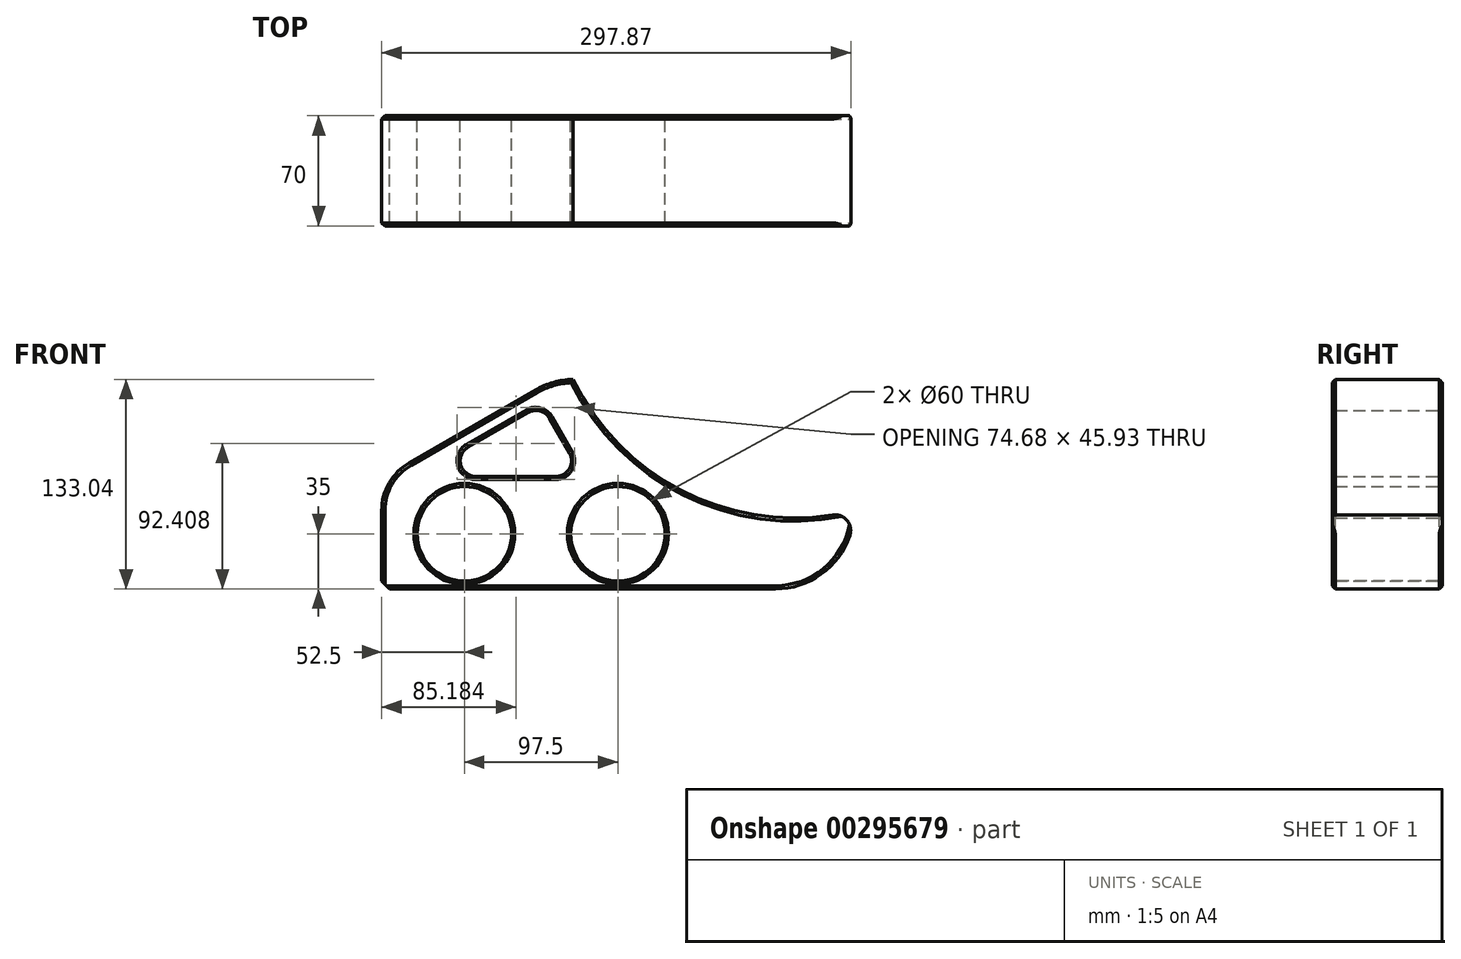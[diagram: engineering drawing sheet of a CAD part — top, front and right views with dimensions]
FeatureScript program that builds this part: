
annotation { "Feature Type Name" : "Feature", "Feature Type Description" : "" }
export const myFeature = defineFeature(function(context is Context, id is Id, definition is map)
    precondition{}
    {
        {
            var Q0;
            Q0=qCreatedBy(makeId("Front.planeOp"),FACE);
            var sketch = newSketch(context, id + "F0", { "sketchPlane" : qUnion([Q0])});
            skLineSegment(sketch, "E0", {"start": v(-157.76, 0) * mm, "end": v(158.79, 0) * mm, "construction": true});
            skLineSegment(sketch, "E1.bottom", {"start": v(150, -35) * mm, "end": v(-150, -35) * mm});
            skLineSegment(sketch, "E1.left", {"start": v(150, -35) * mm, "end": v(150, 14.8) * mm});
            skLineSegment(sketch, "E1.right", {"start": v(-150, -35) * mm, "end": v(-150, 14.8) * mm});
            skPoint(sketch, "E1.middle", {"position": v(0, 0) * mm});
            skCircle(sketch, "E2", {"center": v(0, 0) * mm, "radius": 30 * mm});
            skLineSegment(sketch, "E3", {"start": v(-132.5, 45.1) * mm, "end": v(-52.4, 91.35) * mm});
            skArc(sketch, "E4.filletArc", {"start": v(-132.5, 45.1) * mm, "mid": v(-145.31, 32.3) * mm, "end": v(-150, 14.8) * mm});
            skPoint(sketch, "E5.visualSharp", {"position": v(-41.9, 97.42) * mm});
            skArc(sketch, "E5.filletArc", {"start": v(-28.5, 98.04) * mm, "mid": v(-40.87, 96.2) * mm, "end": v(-52.4, 91.35) * mm});
            skLineSegment(sketch, "E6", {"start": v(0, 102.38) * mm, "end": v(0, -61.25) * mm, "construction": true});
            skLineSegment(sketch, "E7", {"start": v(0, 0) * mm, "end": v(-97.5, 0) * mm, "construction": true});
            skPoint(sketch, "E8", {"position": v(-97.5, 0) * mm});
            skCircle(sketch, "E9", {"center": v(-97.5, 0) * mm, "radius": 30 * mm});
            skLineSegment(sketch, "E10.0", {"start": v(-95.18, 55.1) * mm, "end": v(-57.15, 77.06) * mm});
            skLineSegment(sketch, "E11", {"start": v(-43.5, 73.4) * mm, "end": v(-30.82, 51.44) * mm});
            skLineSegment(sketch, "E12", {"start": v(-90.18, 36.44) * mm, "end": v(-39.48, 36.44) * mm});
            skPoint(sketch, "E13.visualSharp", {"position": v(-48.5, 82.06) * mm});
            skArc(sketch, "E13.filletArc", {"start": v(-43.5, 73.4) * mm, "mid": v(-49.57, 78.06) * mm, "end": v(-57.15, 77.06) * mm});
            skArc(sketch, "E14.filletArc", {"start": v(-39.48, 36.44) * mm, "mid": v(-30.82, 41.44) * mm, "end": v(-30.82, 51.44) * mm});
            skPoint(sketch, "E15.visualSharp", {"position": v(0, 38.68) * mm});
            skPoint(sketch, "E16.newPointA", {"position": v(48.5, 82.06) * mm});
            skPoint(sketch, "E17.visualSharp", {"position": v(-127.5, 36.44) * mm});
            skArc(sketch, "E17.filletArc", {"start": v(-95.18, 55.1) * mm, "mid": v(-99.84, 43.86) * mm, "end": v(-90.18, 36.44) * mm});
            skPoint(sketch, "E18.visualSharp", {"position": v(127.5, 36.44) * mm});
            skArc(sketch, "E19", {"start": v(-28.5, 98.04) * mm, "mid": v(45.97, 24.73) * mm, "end": v(150, 14.8) * mm});
            skSolve(sketch);
        }
        {
            var Q0;
            Q0 = qSketchRegion(id + "F0", true);
            extrude(context, id + "F1", {"entities" : qUnion([Q0]), "depth" : 70 * mm, "symmetric" : true});
        }
        {
            var Q0;
            Q0=makeQuery(id+"F1.opExtrude","SWEPT_EDGE",EDGE,{"disambiguationData":[OSD([sQuery(id+"F0.wireOp",EDGE,"E1.bottom"),sQuery(id+"F0.wireOp",EDGE,"E1.left")])]});
            fillet(context, id + "F2", {"entities" : qUnion([Q0]), "radius" : 50 * mm, "tangentPropagation" : true, "allowEdgeOverflow" : false});
        }
        {
            var Q0;
            Q0=makeQuery(id+"F1.opExtrude","CAP_FACE",FACE,{"disambiguationData":[OSD([sQuery(id+"F0.wireOp",EDGE,"E1.bottom"),sQuery(id+"F0.wireOp",EDGE,"E1.left"),sQuery(id+"F0.wireOp",EDGE,"E1.right"),sQuery(id+"F0.wireOp",EDGE,"E2"),sQuery(id+"F0.wireOp",EDGE,"E3"),sQuery(id+"F0.wireOp",EDGE,"E4.filletArc"),sQuery(id+"F0.wireOp",EDGE,"E5.filletArc"),sQuery(id+"F0.wireOp",EDGE,"2128d712-c22e-43d0-b137-ae846bd3470c0.MirrorCS"),sQuery(id+"F0.wireOp",EDGE,"ead384d1-ae69-4692-b830-1a13f9f5a69b0.MirrorCS"),sQuery(id+"F0.wireOp",EDGE,"37f9a7ff-8684-4468-8a72-e05079eaa0670.MirrorCS"),sQuery(id+"F0.wireOp",EDGE,"Lrirhn2S-7brx-2jdC-clf1-sQWSoA0U2pV4"),sQuery(id+"F0.wireOp",EDGE,"E9"),sQuery(id+"F0.wireOp",EDGE,"E10.0"),sQuery(id+"F0.wireOp",EDGE,"fc2dcb0f-4b4e-4361-bf83-8e2945b27883.0"),sQuery(id+"F0.wireOp",EDGE,"da70da69-e66b-4109-82d2-453cd6daba01.0"),sQuery(id+"F0.wireOp",EDGE,"AouGleSv-KkGm-sB8C-ZEsv-O4xofjI2ggc6"),sQuery(id+"F0.wireOp",EDGE,"E11"),sQuery(id+"F0.wireOp",EDGE,"E12"),sQuery(id+"F0.wireOp",EDGE,"ibZBRqrK-dixR-fJSc-eGvf-ZQZpcMRPZl58"),sQuery(id+"F0.wireOp",EDGE,"4ea5772b-329a-4e50-88f7-68c20ca4a20b0.MirrorCS"),sQuery(id+"F0.wireOp",EDGE,"01e6399d-9f67-49b3-929a-f7497086e1730.MirrorCS"),sQuery(id+"F0.wireOp",EDGE,"E13.filletArc"),sQuery(id+"F0.wireOp",EDGE,"E14.filletArc"),sQuery(id+"F0.wireOp",EDGE,"E15.filletArc"),sQuery(id+"F0.wireOp",EDGE,"7a9b99ec-dd7e-44b2-9577-c392ffdbf900.filletArc"),sQuery(id+"F0.wireOp",EDGE,"3fdbf697-db4c-413a-9f31-464b24b49e91.filletArc"),sQuery(id+"F0.wireOp",EDGE,"E16.filletArc"),sQuery(id+"F0.wireOp",EDGE,"00bd977d-d024-4b05-abdb-e15cf0350885.filletArc"),sQuery(id+"F0.wireOp",EDGE,"E17.filletArc"),sQuery(id+"F0.wireOp",EDGE,"E18.filletArc")])],"isStart":false});
            var Q1;
            Q1=makeQuery(id+"F1.opExtrude","CAP_FACE",FACE,{"disambiguationData":[OSD([sQuery(id+"F0.wireOp",EDGE,"E1.bottom"),sQuery(id+"F0.wireOp",EDGE,"E1.left"),sQuery(id+"F0.wireOp",EDGE,"E1.right"),sQuery(id+"F0.wireOp",EDGE,"E2"),sQuery(id+"F0.wireOp",EDGE,"E3"),sQuery(id+"F0.wireOp",EDGE,"E4.filletArc"),sQuery(id+"F0.wireOp",EDGE,"E5.filletArc"),sQuery(id+"F0.wireOp",EDGE,"2128d712-c22e-43d0-b137-ae846bd3470c0.MirrorCS"),sQuery(id+"F0.wireOp",EDGE,"ead384d1-ae69-4692-b830-1a13f9f5a69b0.MirrorCS"),sQuery(id+"F0.wireOp",EDGE,"37f9a7ff-8684-4468-8a72-e05079eaa0670.MirrorCS"),sQuery(id+"F0.wireOp",EDGE,"Lrirhn2S-7brx-2jdC-clf1-sQWSoA0U2pV4"),sQuery(id+"F0.wireOp",EDGE,"E9"),sQuery(id+"F0.wireOp",EDGE,"E10.0"),sQuery(id+"F0.wireOp",EDGE,"fc2dcb0f-4b4e-4361-bf83-8e2945b27883.0"),sQuery(id+"F0.wireOp",EDGE,"da70da69-e66b-4109-82d2-453cd6daba01.0"),sQuery(id+"F0.wireOp",EDGE,"AouGleSv-KkGm-sB8C-ZEsv-O4xofjI2ggc6"),sQuery(id+"F0.wireOp",EDGE,"E11"),sQuery(id+"F0.wireOp",EDGE,"E12"),sQuery(id+"F0.wireOp",EDGE,"ibZBRqrK-dixR-fJSc-eGvf-ZQZpcMRPZl58"),sQuery(id+"F0.wireOp",EDGE,"4ea5772b-329a-4e50-88f7-68c20ca4a20b0.MirrorCS"),sQuery(id+"F0.wireOp",EDGE,"01e6399d-9f67-49b3-929a-f7497086e1730.MirrorCS"),sQuery(id+"F0.wireOp",EDGE,"E13.filletArc"),sQuery(id+"F0.wireOp",EDGE,"E14.filletArc"),sQuery(id+"F0.wireOp",EDGE,"E15.filletArc"),sQuery(id+"F0.wireOp",EDGE,"7a9b99ec-dd7e-44b2-9577-c392ffdbf900.filletArc"),sQuery(id+"F0.wireOp",EDGE,"3fdbf697-db4c-413a-9f31-464b24b49e91.filletArc"),sQuery(id+"F0.wireOp",EDGE,"E16.filletArc"),sQuery(id+"F0.wireOp",EDGE,"00bd977d-d024-4b05-abdb-e15cf0350885.filletArc"),sQuery(id+"F0.wireOp",EDGE,"E17.filletArc"),sQuery(id+"F0.wireOp",EDGE,"E18.filletArc")])],"isStart":true});
            chamfer(context, id + "F3", {"entities" : qUnion([Q0, Q1]), "width" : 2 * mm, "tangentPropagation" : true});
        }
        {
            var Q0;
            Q0=makeQuery(id+"F1.opExtrude","SWEPT_EDGE",EDGE,{"disambiguationData":[OSD([sQuery(id+"F0.wireOp",EDGE,"E1.bottom"),sQuery(id+"F0.wireOp",EDGE,"E1.right")])]});
            chamfer(context, id + "F4", {"entities" : qUnion([Q0]), "width" : 5 * mm, "tangentPropagation" : true});
        }
        {
            var Q0;
            Q0=makeQuery(id+"F2.opFillet","BLEND_EDGE",EDGE,{"blendedFrom":[makeQuery(id+"F1.opExtrude","SWEPT_EDGE",EDGE,{"disambiguationData":[OSD([sQuery(id+"F0.wireOp",EDGE,"E1.bottom"),sQuery(id+"F0.wireOp",EDGE,"E1.left")])]}),makeQuery(id+"F1.opExtrude","SWEPT_FACE",FACE,{"disambiguationData":[OSD([sQuery(id+"F0.wireOp",EDGE,"E19")])]})],"blendedInto":[makeQuery(id+"F1.opExtrude","SWEPT_FACE",FACE,{"disambiguationData":[OSD([sQuery(id+"F0.wireOp",EDGE,"E19")])]})]});
            fillet(context, id + "F5", {"entities" : qUnion([Q0]), "radius" : 10 * mm, "tangentPropagation" : true, "allowEdgeOverflow" : false});
        }
    });
